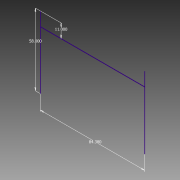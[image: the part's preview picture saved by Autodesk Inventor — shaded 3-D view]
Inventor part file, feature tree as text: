
AUTODESK INVENTOR PART (.ipt)
format: ipt  version: 2013 (Build 170138000, 138)  size: 61,440 bytes
history: native  units: in
note: dims shown in document units (in); Inventor stores cm internally (conversion verified against a paired STEP export)
features: sketch x1
ambient origin geometry x8: Origin, YZ Plane, XZ Plane, XY Plane, X Axis, Y Axis, Z Axis, Center Point
feature tree (1):
  sketch  "Sketch1"  dims[d0=58.0in d1=84.38in d2=11.0in]
